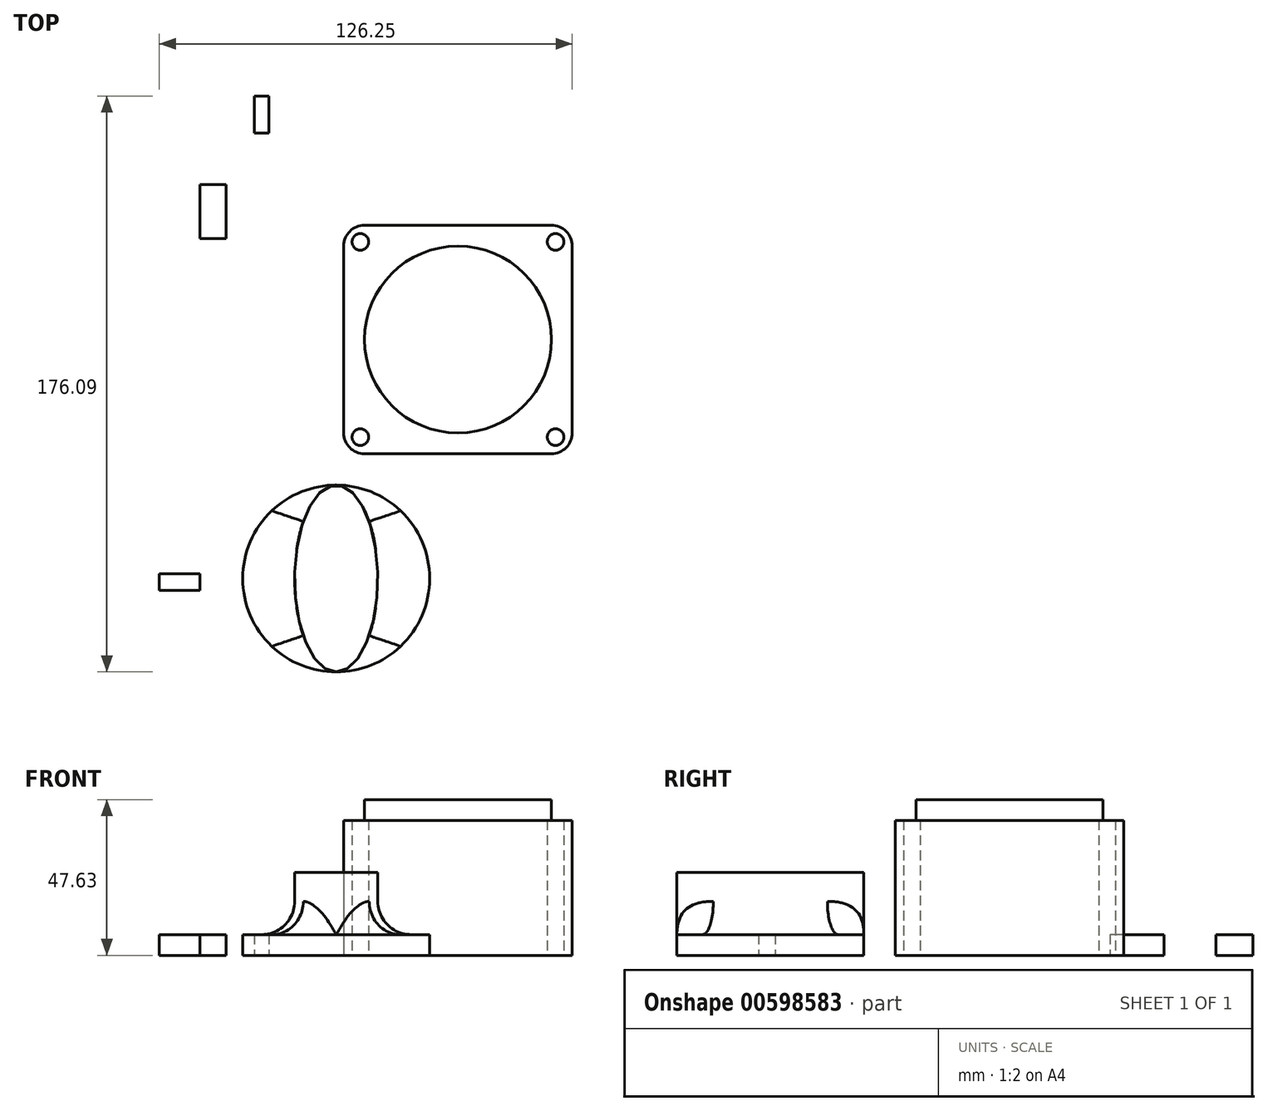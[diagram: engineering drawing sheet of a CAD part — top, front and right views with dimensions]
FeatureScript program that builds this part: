
annotation { "Feature Type Name" : "Feature", "Feature Type Description" : "" }
export const myFeature = defineFeature(function(context is Context, id is Id, definition is map)
    precondition{}
    {
        {
            var Q0;
            Q0=qCreatedBy(makeId("Top.planeOp"),FACE);
            var sketch = newSketch(context, id + "F0", { "sketchPlane" : qUnion([Q0])});
            skLineSegment(sketch, "E0.bottom", {"start": v(-30.56, -28.81) * mm, "end": v(39.29, -28.81) * mm});
            skLineSegment(sketch, "E0.top", {"start": v(-30.56, 41.04) * mm, "end": v(39.29, 41.04) * mm});
            skLineSegment(sketch, "E0.left", {"start": v(-30.56, -28.81) * mm, "end": v(-30.56, 41.04) * mm});
            skLineSegment(sketch, "E0.right", {"start": v(39.29, -28.81) * mm, "end": v(39.29, 41.04) * mm});
            skCircle(sketch, "E1", {"center": v(34.2, 35.96) * mm, "radius": 2.54 * mm});
            skCircle(sketch, "E2", {"center": v(34.2, -23.73) * mm, "radius": 2.54 * mm});
            skCircle(sketch, "E3", {"center": v(-25.48, 35.96) * mm, "radius": 2.54 * mm});
            skCircle(sketch, "E4", {"center": v(-25.48, -23.73) * mm, "radius": 2.54 * mm});
            skSolve(sketch);
        }
        {
            var Q0;
            Q0 = qSketchRegion(id + "F0", true);
            extrude(context, id + "F1", {"entities" : qUnion([Q0]), "depth" : 41.27 * mm, "offsetDistance" : 25.4 * mm});
        }
        {
            var Q0;
            Q0=makeQuery(id+"F1.opExtrude","CAP_FACE",FACE,{"disambiguationData":[OSD([sQuery(id+"F0.wireOp",EDGE,"E0.bottom"),sQuery(id+"F0.wireOp",EDGE,"E0.top"),sQuery(id+"F0.wireOp",EDGE,"E0.left"),sQuery(id+"F0.wireOp",EDGE,"E0.right")])],"isStart":false});
            var sketch = newSketch(context, id + "F2", { "sketchPlane" : qUnion([Q0])});
            skCircle(sketch, "E5", {"center": v(4.36, 6.11) * mm, "radius": 28.58 * mm});
            skPoint(sketch, "E5.centerSnap0", {"position": v(39.29, 6.11) * mm});
            skPoint(sketch, "E5.centerSnap1", {"position": v(4.36, 41.04) * mm});
            skSolve(sketch);
        }
        {
            var Q0;
            Q0 = qSketchRegion(id + "F2", true);
            extrude(context, id + "F3", {"entities" : qUnion([Q0]), "operationType" : NewBodyOperationType.ADD, "depth" : 6.35 * mm, "offsetDistance" : 25.4 * mm});
        }
        {
            var Q0;
            Q0=makeQuery(id+"F1.opExtrude","SWEPT_EDGE",EDGE,{"disambiguationData":[OSD([sQuery(id+"F0.wireOp",EDGE,"E0.bottom"),sQuery(id+"F0.wireOp",EDGE,"E0.right")])]});
            var Q1;
            Q1=makeQuery(id+"F1.opExtrude","SWEPT_EDGE",EDGE,{"disambiguationData":[OSD([sQuery(id+"F0.wireOp",EDGE,"E0.bottom"),sQuery(id+"F0.wireOp",EDGE,"E0.left")])]});
            var Q2;
            Q2=makeQuery(id+"F1.opExtrude","SWEPT_EDGE",EDGE,{"disambiguationData":[OSD([sQuery(id+"F0.wireOp",EDGE,"E0.top"),sQuery(id+"F0.wireOp",EDGE,"E0.left")])]});
            var Q3;
            Q3=makeQuery(id+"F1.opExtrude","SWEPT_EDGE",EDGE,{"disambiguationData":[OSD([sQuery(id+"F0.wireOp",EDGE,"E0.top"),sQuery(id+"F0.wireOp",EDGE,"E0.right")])]});
            fillet(context, id + "F4", {"entities" : qUnion([Q0, Q1, Q2, Q3]), "radius" : 6.35 * mm, "tangentPropagation" : true, "allowEdgeOverflow" : false});
        }
        {
            var Q0;
            Q0=qCreatedBy(makeId("Top.planeOp"),FACE);
            var sketch = newSketch(context, id + "F5", { "sketchPlane" : qUnion([Q0])});
            skLineSegment(sketch, "E6.bottom", {"start": v(-57.92, 69.2) * mm, "end": v(-53.49, 69.2) * mm});
            skLineSegment(sketch, "E6.top", {"start": v(-57.92, 80.54) * mm, "end": v(-53.49, 80.54) * mm});
            skLineSegment(sketch, "E6.left", {"start": v(-57.92, 69.2) * mm, "end": v(-57.92, 80.54) * mm});
            skLineSegment(sketch, "E6.right", {"start": v(-53.49, 69.2) * mm, "end": v(-53.49, 80.54) * mm});
            skLineSegment(sketch, "E7.bottom", {"start": v(-66.48, 53.42) * mm, "end": v(-74.56, 53.42) * mm});
            skLineSegment(sketch, "E7.top", {"start": v(-66.48, 36.93) * mm, "end": v(-74.56, 36.93) * mm});
            skLineSegment(sketch, "E7.left", {"start": v(-66.48, 53.42) * mm, "end": v(-66.48, 36.93) * mm});
            skLineSegment(sketch, "E7.right", {"start": v(-74.56, 53.42) * mm, "end": v(-74.56, 36.93) * mm});
            skLineSegment(sketch, "E8.bottom", {"start": v(-74.56, -65.46) * mm, "end": v(-86.96, -65.46) * mm});
            skLineSegment(sketch, "E8.top", {"start": v(-74.56, -70.55) * mm, "end": v(-86.96, -70.55) * mm});
            skLineSegment(sketch, "E8.left", {"start": v(-74.56, -65.46) * mm, "end": v(-74.56, -70.55) * mm});
            skLineSegment(sketch, "E8.right", {"start": v(-86.96, -65.46) * mm, "end": v(-86.96, -70.55) * mm});
            skCircle(sketch, "E9", {"center": v(-32.86, -66.97) * mm, "radius": 28.58 * mm});
            skSolve(sketch);
        }
        {
            var Q0;
            Q0 = qSketchRegion(id + "F5", true);
            extrude(context, id + "F6", {"entities" : qUnion([Q0]), "depth" : 6.35 * mm, "offsetDistance" : 25.4 * mm});
        }
        {
            var Q0;
            Q0=makeQuery(id+"F6.opExtrude","CAP_FACE",FACE,{"disambiguationData":[OSD([sQuery(id+"F5.wireOp",EDGE,"E9")])],"isStart":false});
            var sketch = newSketch(context, id + "F7", { "sketchPlane" : qUnion([Q0])});
            skEllipse(sketch, "E10", {"center": v(-32.86, -66.97) * mm, "majorRadius": 28.58 * mm, "minorRadius": 12.7 * mm, "majorAxis": v(0, -1)});
            skSolve(sketch);
        }
        {
            var Q0;
            Q0 = qSketchRegion(id + "F7", true);
            extrude(context, id + "F8", {"entities" : qUnion([Q0]), "operationType" : NewBodyOperationType.ADD, "depth" : 19.05 * mm, "offsetDistance" : 25.4 * mm});
        }
        {
            var Q0;
            Q0=makeQuery(id+"F8.boolean.opBoolean","SPLIT",EDGE,{"disambiguationData":[OD(0.0)],"derivedFrom":makeQuery(id+"F8.opExtrude","CAP_EDGE",EDGE,{"disambiguationData":[OSD([sQuery(id+"F7.wireOp",EDGE,"E10")])],"isStart":true})});
            fillet(context, id + "F9", {"entities" : qUnion([Q0]), "radius" : 10.16 * mm, "tangentPropagation" : true, "allowEdgeOverflow" : false});
        }
    });
